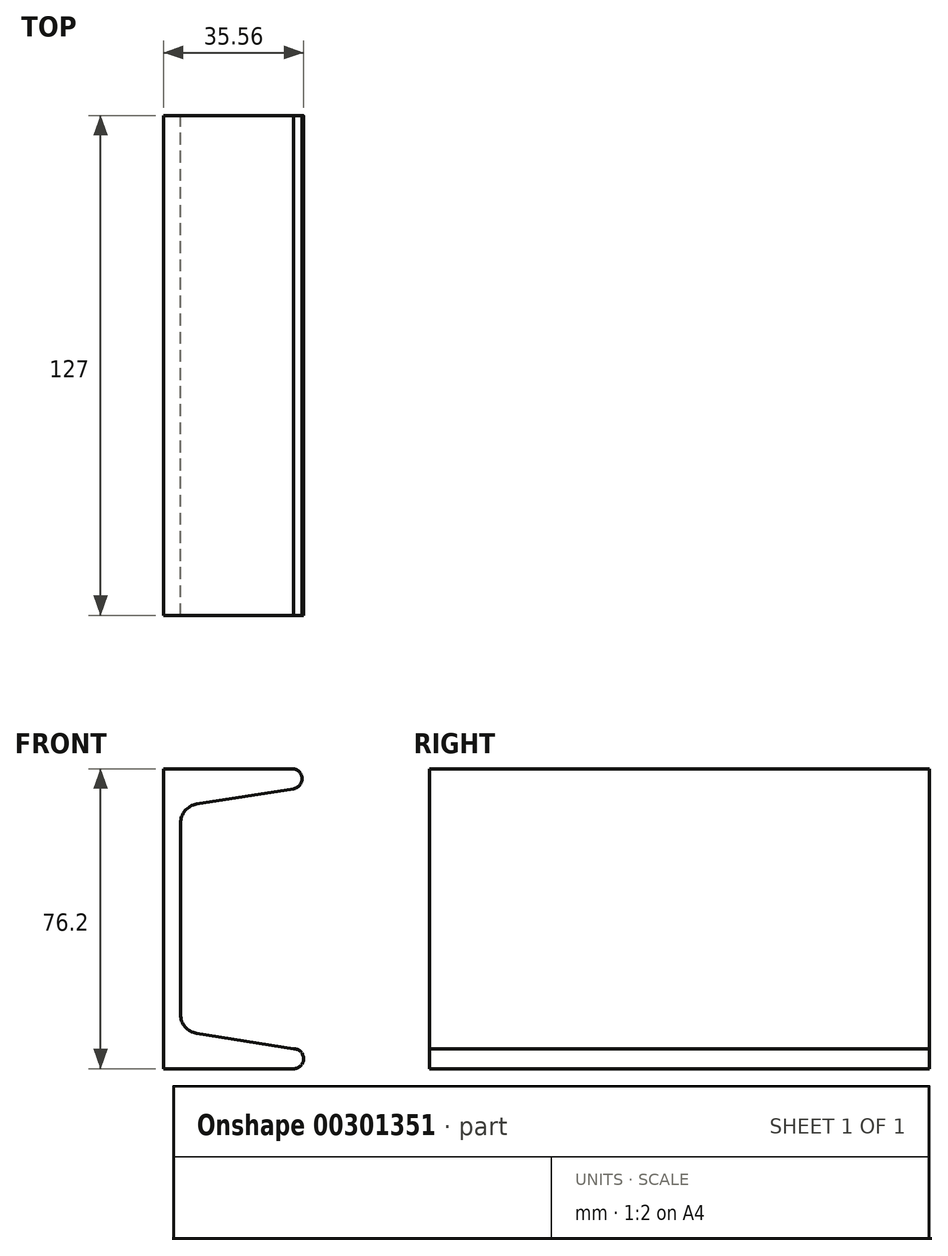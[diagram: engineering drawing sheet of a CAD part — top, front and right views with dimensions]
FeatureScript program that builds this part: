
annotation { "Feature Type Name" : "Feature", "Feature Type Description" : "" }
export const myFeature = defineFeature(function(context is Context, id is Id, definition is map)
    precondition{}
    {
        {
            var Q0;
            Q0=qCreatedBy(makeId("Front.planeOp"),FACE);
            var sketch = newSketch(context, id + "F0", { "sketchPlane" : qUnion([Q0])});
            skLineSegment(sketch, "E0", {"start": v(0, 0) * mm, "end": v(0, 76.2) * mm});
            skLineSegment(sketch, "E1", {"start": v(0, 76.2) * mm, "end": v(33.02, 76.2) * mm});
            skLineSegment(sketch, "E2", {"start": v(4.32, 62.43) * mm, "end": v(4.32, 13.77) * mm});
            skLineSegment(sketch, "E3", {"start": v(33.02, 0) * mm, "end": v(0, 0) * mm});
            skLineSegment(sketch, "E4", {"start": v(33.02, 71.12) * mm, "end": v(8.41, 67.22) * mm});
            skLineSegment(sketch, "E5", {"start": v(33.02, 5.08) * mm, "end": v(8.41, 8.98) * mm});
            skArc(sketch, "E6", {"start": v(33.02, 0) * mm, "mid": v(35.56, 2.54) * mm, "end": v(33.02, 5.08) * mm});
            skArc(sketch, "E7", {"start": v(33.02, 71.12) * mm, "mid": v(35.19, 73.66) * mm, "end": v(33.02, 76.2) * mm});
            skPoint(sketch, "E8.visualSharp", {"position": v(4.32, 9.63) * mm});
            skArc(sketch, "E8.filletArc", {"start": v(4.32, 13.77) * mm, "mid": v(5.48, 10.62) * mm, "end": v(8.41, 8.98) * mm});
            skPoint(sketch, "E9.visualSharp", {"position": v(4.32, 66.57) * mm});
            skArc(sketch, "E9.filletArc", {"start": v(8.41, 67.22) * mm, "mid": v(5.48, 65.58) * mm, "end": v(4.32, 62.43) * mm});
            skSolve(sketch);
        }
        {
            var Q0;
            Q0 = qSketchRegion(id + "F0", true);
            extrude(context, id + "F1", {"entities" : qUnion([Q0]), "depth" : 127 * mm});
        }
    });
